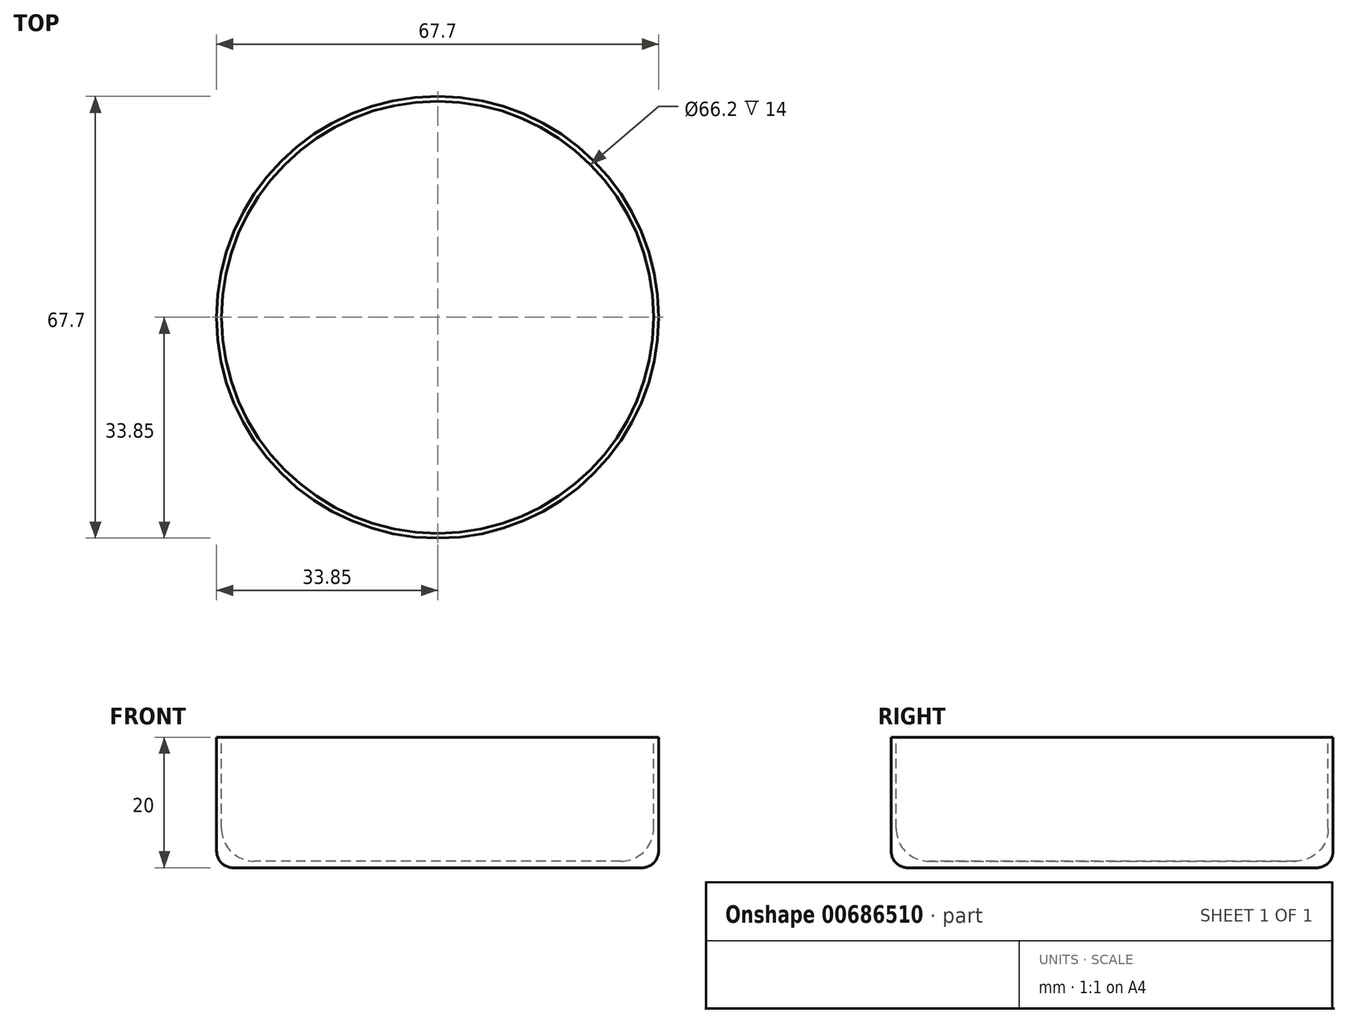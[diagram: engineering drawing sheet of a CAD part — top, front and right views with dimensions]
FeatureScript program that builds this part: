
annotation { "Feature Type Name" : "Feature", "Feature Type Description" : "" }
export const myFeature = defineFeature(function(context is Context, id is Id, definition is map)
    precondition{}
    {
        {
            var Q0;
            Q0=qCreatedBy(makeId("Top.planeOp"),FACE);
            var sketch = newSketch(context, id + "F0", { "sketchPlane" : qUnion([Q0])});
            skCircle(sketch, "E0", {"center": v(0, 0) * mm, "radius": 33.85 * mm});
            skSolve(sketch);
        }
        {
            var Q0;
            Q0=makeQuery(id+"F0.imprint","IMPRINT",FACE,{"disambiguationData":[TD([[makeQuery(id+"F0.imprint","IMPRINT",EDGE,{"derivedFrom":sQuery(id+"F0.wireOp",EDGE,"E0")}),1.0]])]});
            extrude(context, id + "F1", {"entities" : qUnion([Q0]), "depth" : 20 * mm, "offsetDistance" : 25 * mm});
        }
        {
            var Q0;
            Q0=makeQuery(id+"F1.opExtrude","CAP_FACE",FACE,{"disambiguationData":[OSD([sQuery(id+"F0.wireOp",EDGE,"E0")])],"isStart":false});
            var sketch = newSketch(context, id + "F2", { "sketchPlane" : qUnion([Q0])});
            skCircle(sketch, "E1", {"center": v(0, 0) * mm, "radius": 33.1 * mm});
            skSolve(sketch);
        }
        {
            var Q0;
            Q0=makeQuery(id+"F2.imprint","IMPRINT",FACE,{"disambiguationData":[TD([[makeQuery(id+"F2.imprint","IMPRINT",EDGE,{"derivedFrom":sQuery(id+"F2.wireOp",EDGE,"E1")}),1.0]])]});
            extrude(context, id + "F3", {"entities" : qUnion([Q0]), "operationType" : NewBodyOperationType.REMOVE, "oppositeDirection" : true, "depth" : 19 * mm, "offsetDistance" : 25 * mm});
        }
        {
            var Q0;
            Q0=makeQuery(id+"F3.boolean.opBoolean","COPY",FACE,{"derivedFrom":makeQuery(id+"F3.opExtrude","CAP_FACE",FACE,{"disambiguationData":[OSD([sQuery(id+"F2.wireOp",EDGE,"E1")])],"isStart":false})});
            fillet(context, id + "F4", {"entities" : qUnion([Q0]), "radius" : 5 * mm, "tangentPropagation" : true, "allowEdgeOverflow" : false});
        }
        {
            var Q0;
            Q0=makeQuery(id+"F1.opExtrude","CAP_FACE",FACE,{"disambiguationData":[OSD([sQuery(id+"F0.wireOp",EDGE,"E0")])],"isStart":true});
            fillet(context, id + "F5", {"entities" : qUnion([Q0]), "radius" : 2.5 * mm, "tangentPropagation" : true, "allowEdgeOverflow" : false});
        }
    });
